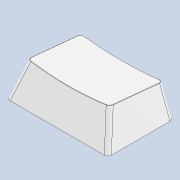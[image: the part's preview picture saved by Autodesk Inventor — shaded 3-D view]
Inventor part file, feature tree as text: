
AUTODESK INVENTOR PART (.ipt)
format: ipt  version: 2021 (Build 250183000, 183)  size: 245,248 bytes
history: native  units: in
note: dims shown in document units (in); Inventor stores cm internally (conversion verified against a paired STEP export)
features: chamfer x1
ambient origin geometry x8: Origin, YZ Plane, XZ Plane, XY Plane, X Axis, Y Axis, Z Axis, Center Point
bodies: Solid1 (feature_tree)
feature tree (1):
  chamfer  "Chamfer1"  [1 undecoded]
note: 1 required parameter value undecoded (feature->parameter linkage not recoverable at this tier; creation-order binding heuristic only, values carry confidence <= 0.55)
